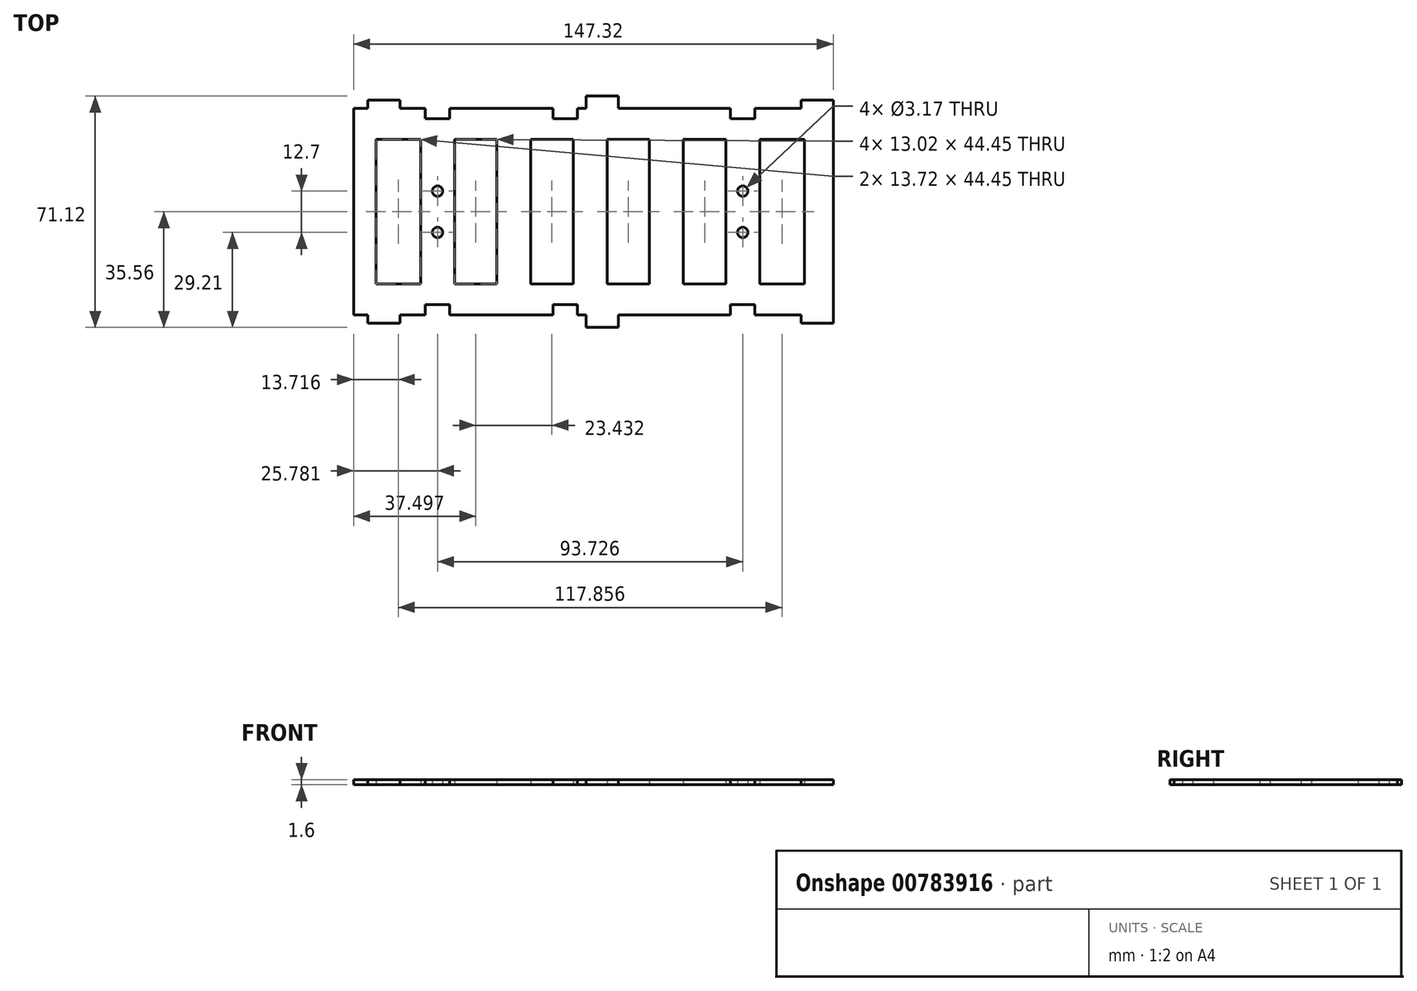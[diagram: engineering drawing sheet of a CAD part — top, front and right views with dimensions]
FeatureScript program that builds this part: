
annotation { "Feature Type Name" : "Feature", "Feature Type Description" : "" }
export const myFeature = defineFeature(function(context is Context, id is Id, definition is map)
    precondition{}
    {
        {
            var Q0;
            Q0=qCreatedBy(makeId("Top.planeOp"),FACE);
            var sketch = newSketch(context, id + "F0", { "sketchPlane" : qUnion([Q0])});
            skLineSegment(sketch, "E0.bottom", {"start": v(63.75, 31.75) * mm, "end": v(49.6, 31.75) * mm});
            skLineSegment(sketch, "E0.top", {"start": v(63.75, -31.75) * mm, "end": v(49.6, -31.75) * mm});
            skLineSegment(sketch, "E0.left", {"start": v(73.66, 31.75) * mm, "end": v(73.66, -31.75) * mm});
            skLineSegment(sketch, "E0.right", {"start": v(-73.66, 31.75) * mm, "end": v(-73.66, -31.75) * mm});
            skLineSegment(sketch, "E1.bottom", {"start": v(-53.09, 22.22) * mm, "end": v(-66.8, 22.22) * mm});
            skLineSegment(sketch, "E1.top", {"start": v(-53.09, -22.23) * mm, "end": v(-66.8, -22.23) * mm});
            skLineSegment(sketch, "E1.left", {"start": v(-53.09, 22.23) * mm, "end": v(-53.09, -22.23) * mm});
            skLineSegment(sketch, "E1.right", {"start": v(-66.8, 22.23) * mm, "end": v(-66.8, -22.23) * mm});
            skPoint(sketch, "E1.middle", {"position": v(-59.94, 0) * mm});
            skLineSegment(sketch, "E2", {"start": v(-69.34, 31.75) * mm, "end": v(-69.34, 34.3) * mm});
            skLineSegment(sketch, "E3", {"start": v(-69.34, 34.3) * mm, "end": v(-59.44, 34.3) * mm});
            skLineSegment(sketch, "E4", {"start": v(-59.44, 34.3) * mm, "end": v(-59.44, 31.75) * mm});
            skLineSegment(sketch, "E5", {"start": v(73.66, 31.75) * mm, "end": v(73.66, 34.3) * mm});
            skLineSegment(sketch, "E6", {"start": v(73.66, 34.3) * mm, "end": v(63.75, 34.3) * mm});
            skLineSegment(sketch, "E7", {"start": v(63.75, 34.3) * mm, "end": v(63.75, 31.75) * mm});
            skLineSegment(sketch, "E8", {"start": v(-2.29, 31.75) * mm, "end": v(-2.29, 35.56) * mm});
            skLineSegment(sketch, "E9", {"start": v(-2.29, 35.56) * mm, "end": v(7.62, 35.56) * mm});
            skLineSegment(sketch, "E10", {"start": v(7.62, 35.56) * mm, "end": v(7.62, 31.75) * mm});
            skLineSegment(sketch, "E11.MirrorCS", {"start": v(-69.34, -31.75) * mm, "end": v(-69.34, -34.3) * mm});
            skLineSegment(sketch, "E12.MirrorCS", {"start": v(-69.34, -34.3) * mm, "end": v(-59.44, -34.3) * mm});
            skLineSegment(sketch, "E13.MirrorCS", {"start": v(-59.44, -34.3) * mm, "end": v(-59.44, -31.75) * mm});
            skLineSegment(sketch, "E14.MirrorCS", {"start": v(-2.29, -31.75) * mm, "end": v(-2.29, -35.56) * mm});
            skLineSegment(sketch, "E15.MirrorCS", {"start": v(-2.29, -35.56) * mm, "end": v(7.62, -35.56) * mm});
            skLineSegment(sketch, "E16.MirrorCS", {"start": v(7.62, -35.56) * mm, "end": v(7.62, -31.75) * mm});
            skLineSegment(sketch, "E17.MirrorCS", {"start": v(63.75, -34.3) * mm, "end": v(63.75, -31.75) * mm});
            skLineSegment(sketch, "E18.MirrorCS", {"start": v(73.66, -34.3) * mm, "end": v(63.75, -34.3) * mm});
            skLineSegment(sketch, "E19.MirrorCS", {"start": v(73.66, -31.75) * mm, "end": v(73.66, -34.3) * mm});
            skLineSegment(sketch, "E20.trimOffspring", {"start": v(-69.34, -31.75) * mm, "end": v(-73.66, -31.75) * mm});
            skLineSegment(sketch, "E21.trimOffspring", {"start": v(-69.34, 31.75) * mm, "end": v(-73.66, 31.75) * mm});
            skLineSegment(sketch, "E22.trimOffspring", {"start": v(-2.29, -31.75) * mm, "end": v(-4.95, -31.75) * mm});
            skLineSegment(sketch, "E23.trimOffspring", {"start": v(-2.29, 31.75) * mm, "end": v(-4.95, 31.75) * mm});
            skLineSegment(sketch, "E24.bottom", {"start": v(-42.67, 22.22) * mm, "end": v(-29.65, 22.22) * mm});
            skLineSegment(sketch, "E24.top", {"start": v(-42.67, -22.23) * mm, "end": v(-29.65, -22.23) * mm});
            skLineSegment(sketch, "E24.left", {"start": v(-42.67, 22.23) * mm, "end": v(-42.67, -22.23) * mm});
            skLineSegment(sketch, "E24.right", {"start": v(-29.65, 22.22) * mm, "end": v(-29.65, -22.23) * mm});
            skPoint(sketch, "E24.middle", {"position": v(-36.16, 0) * mm});
            skLineSegment(sketch, "E25.bottom", {"start": v(-19.24, 22.23) * mm, "end": v(-6.22, 22.23) * mm});
            skLineSegment(sketch, "E25.top", {"start": v(-19.24, -22.23) * mm, "end": v(-6.22, -22.23) * mm});
            skLineSegment(sketch, "E25.left", {"start": v(-19.24, 22.22) * mm, "end": v(-19.24, -22.23) * mm});
            skLineSegment(sketch, "E25.right", {"start": v(-6.22, 22.22) * mm, "end": v(-6.22, -22.23) * mm});
            skPoint(sketch, "E25.middle", {"position": v(-12.73, 0) * mm});
            skLineSegment(sketch, "E26.bottom", {"start": v(4.2, 22.23) * mm, "end": v(17.2, 22.23) * mm});
            skLineSegment(sketch, "E26.top", {"start": v(4.2, -22.23) * mm, "end": v(17.2, -22.23) * mm});
            skLineSegment(sketch, "E26.left", {"start": v(4.2, 22.23) * mm, "end": v(4.2, -22.23) * mm});
            skLineSegment(sketch, "E26.right", {"start": v(17.2, 22.23) * mm, "end": v(17.2, -22.23) * mm});
            skPoint(sketch, "E26.middle", {"position": v(10.7, 0) * mm});
            skLineSegment(sketch, "E27.bottom", {"start": v(27.62, 22.23) * mm, "end": v(40.64, 22.23) * mm});
            skLineSegment(sketch, "E27.top", {"start": v(27.62, -22.22) * mm, "end": v(40.64, -22.22) * mm});
            skLineSegment(sketch, "E27.left", {"start": v(27.62, 22.23) * mm, "end": v(27.62, -22.22) * mm});
            skLineSegment(sketch, "E27.right", {"start": v(40.64, 22.23) * mm, "end": v(40.64, -22.22) * mm});
            skPoint(sketch, "E27.middle", {"position": v(34.13, 0) * mm});
            skLineSegment(sketch, "E28.bottom", {"start": v(51.05, 22.23) * mm, "end": v(64.77, 22.23) * mm});
            skLineSegment(sketch, "E28.top", {"start": v(51.05, -22.22) * mm, "end": v(64.77, -22.22) * mm});
            skLineSegment(sketch, "E28.left", {"start": v(51.05, 22.23) * mm, "end": v(51.05, -22.22) * mm});
            skLineSegment(sketch, "E28.right", {"start": v(64.77, 22.23) * mm, "end": v(64.77, -22.22) * mm});
            skPoint(sketch, "E28.middle", {"position": v(57.91, 0) * mm});
            skLineSegment(sketch, "E29", {"start": v(-53.09, 22.22) * mm, "end": v(-42.67, 22.22) * mm, "construction": true});
            skLineSegment(sketch, "E30", {"start": v(-29.65, 22.22) * mm, "end": v(-19.24, 22.22) * mm, "construction": true});
            skLineSegment(sketch, "E31", {"start": v(-6.22, 22.22) * mm, "end": v(4.2, 22.22) * mm, "construction": true});
            skLineSegment(sketch, "E32", {"start": v(17.2, 22.23) * mm, "end": v(27.62, 22.23) * mm, "construction": true});
            skLineSegment(sketch, "E33", {"start": v(40.64, 22.23) * mm, "end": v(51.05, 22.23) * mm, "construction": true});
            skCircle(sketch, "E34", {"center": v(-47.88, 6.35) * mm, "radius": 1.59 * mm});
            skPoint(sketch, "E34.centerSnap0", {"position": v(-47.88, 22.22) * mm});
            skCircle(sketch, "E35", {"center": v(45.85, 6.35) * mm, "radius": 1.59 * mm});
            skPoint(sketch, "E35.centerSnap0", {"position": v(45.85, 22.23) * mm});
            skCircle(sketch, "E36.MirrorC", {"center": v(-47.88, -6.35) * mm, "radius": 1.59 * mm});
            skCircle(sketch, "E37.MirrorC", {"center": v(45.85, -6.35) * mm, "radius": 1.59 * mm});
            skLineSegment(sketch, "E38", {"start": v(-47.88, 6.35) * mm, "end": v(-47.88, -6.35) * mm, "construction": true});
            skLineSegment(sketch, "E39", {"start": v(45.85, 6.35) * mm, "end": v(45.85, -6.35) * mm, "construction": true});
            skLineSegment(sketch, "E40", {"start": v(-47.88, -28.58) * mm, "end": v(-44.13, -28.58) * mm});
            skLineSegment(sketch, "E41", {"start": v(-44.13, -28.58) * mm, "end": v(-44.13, -31.75) * mm});
            skLineSegment(sketch, "E42", {"start": v(-47.88, -28.58) * mm, "end": v(-51.63, -28.58) * mm});
            skLineSegment(sketch, "E43", {"start": v(-51.63, -28.58) * mm, "end": v(-51.63, -31.75) * mm});
            skLineSegment(sketch, "E44", {"start": v(42.1, -28.58) * mm, "end": v(42.1, -31.75) * mm});
            skLineSegment(sketch, "E45", {"start": v(42.1, -28.58) * mm, "end": v(45.85, -28.58) * mm});
            skLineSegment(sketch, "E46", {"start": v(45.85, -28.58) * mm, "end": v(49.6, -28.58) * mm});
            skLineSegment(sketch, "E47", {"start": v(49.6, -28.58) * mm, "end": v(49.6, -31.75) * mm});
            skLineSegment(sketch, "E48.MirrorCS", {"start": v(-51.63, 28.58) * mm, "end": v(-51.63, 31.75) * mm});
            skLineSegment(sketch, "E49.MirrorCS", {"start": v(-47.88, 28.58) * mm, "end": v(-51.63, 28.58) * mm});
            skLineSegment(sketch, "E50.MirrorCS", {"start": v(-47.88, 28.58) * mm, "end": v(-44.13, 28.58) * mm});
            skLineSegment(sketch, "E51.MirrorCS", {"start": v(-44.13, 28.58) * mm, "end": v(-44.13, 31.75) * mm});
            skLineSegment(sketch, "E52.MirrorCS", {"start": v(42.1, 28.58) * mm, "end": v(42.1, 31.75) * mm});
            skLineSegment(sketch, "E53.MirrorCS", {"start": v(42.1, 28.58) * mm, "end": v(45.85, 28.58) * mm});
            skLineSegment(sketch, "E54.MirrorCS", {"start": v(45.85, 28.58) * mm, "end": v(49.6, 28.58) * mm});
            skLineSegment(sketch, "E55.MirrorCS", {"start": v(49.6, 28.58) * mm, "end": v(49.6, 31.75) * mm});
            skLineSegment(sketch, "E56.trimOffspring", {"start": v(-51.63, 31.75) * mm, "end": v(-59.44, 31.75) * mm});
            skLineSegment(sketch, "E57.trimOffspring", {"start": v(42.1, 31.75) * mm, "end": v(7.62, 31.75) * mm});
            skLineSegment(sketch, "E58.trimOffspring", {"start": v(42.1, -31.75) * mm, "end": v(7.62, -31.75) * mm});
            skLineSegment(sketch, "E59.trimOffspring", {"start": v(-51.63, -31.75) * mm, "end": v(-59.44, -31.75) * mm});
            skLineSegment(sketch, "E60", {"start": v(-12.45, 28.58) * mm, "end": v(-12.45, 31.75) * mm});
            skLineSegment(sketch, "E61", {"start": v(-12.45, 28.58) * mm, "end": v(-8.7, 28.58) * mm});
            skLineSegment(sketch, "E62", {"start": v(-8.7, 28.58) * mm, "end": v(-4.95, 28.58) * mm});
            skLineSegment(sketch, "E63", {"start": v(-4.95, 28.58) * mm, "end": v(-4.95, 31.75) * mm});
            skLineSegment(sketch, "E64.MirrorCS", {"start": v(-12.45, -28.58) * mm, "end": v(-8.7, -28.58) * mm});
            skLineSegment(sketch, "E65.MirrorCS", {"start": v(-8.7, -28.58) * mm, "end": v(-4.95, -28.58) * mm});
            skLineSegment(sketch, "E66.MirrorCS", {"start": v(-4.95, -28.58) * mm, "end": v(-4.95, -31.75) * mm});
            skLineSegment(sketch, "E67.MirrorCS", {"start": v(-12.45, -28.58) * mm, "end": v(-12.45, -31.75) * mm});
            skLineSegment(sketch, "E68.trimOffspring", {"start": v(-12.45, 31.75) * mm, "end": v(-44.13, 31.75) * mm});
            skLineSegment(sketch, "E69.trimOffspring", {"start": v(-12.45, -31.75) * mm, "end": v(-44.13, -31.75) * mm});
            skSolve(sketch);
        }
        {
            var Q0;
            Q0=makeQuery(id+"F0.imprint","IMPRINT",FACE,{"disambiguationData":[TD([[makeQuery(id+"F0.imprint","IMPRINT",EDGE,{"derivedFrom":sQuery(id+"F0.wireOp",EDGE,"E0.bottom")}),1.0]])]});
            extrude(context, id + "F1", {"entities" : qUnion([Q0]), "depth" : 1.6 * mm, "offsetDistance" : 25.4 * mm});
        }
    });
